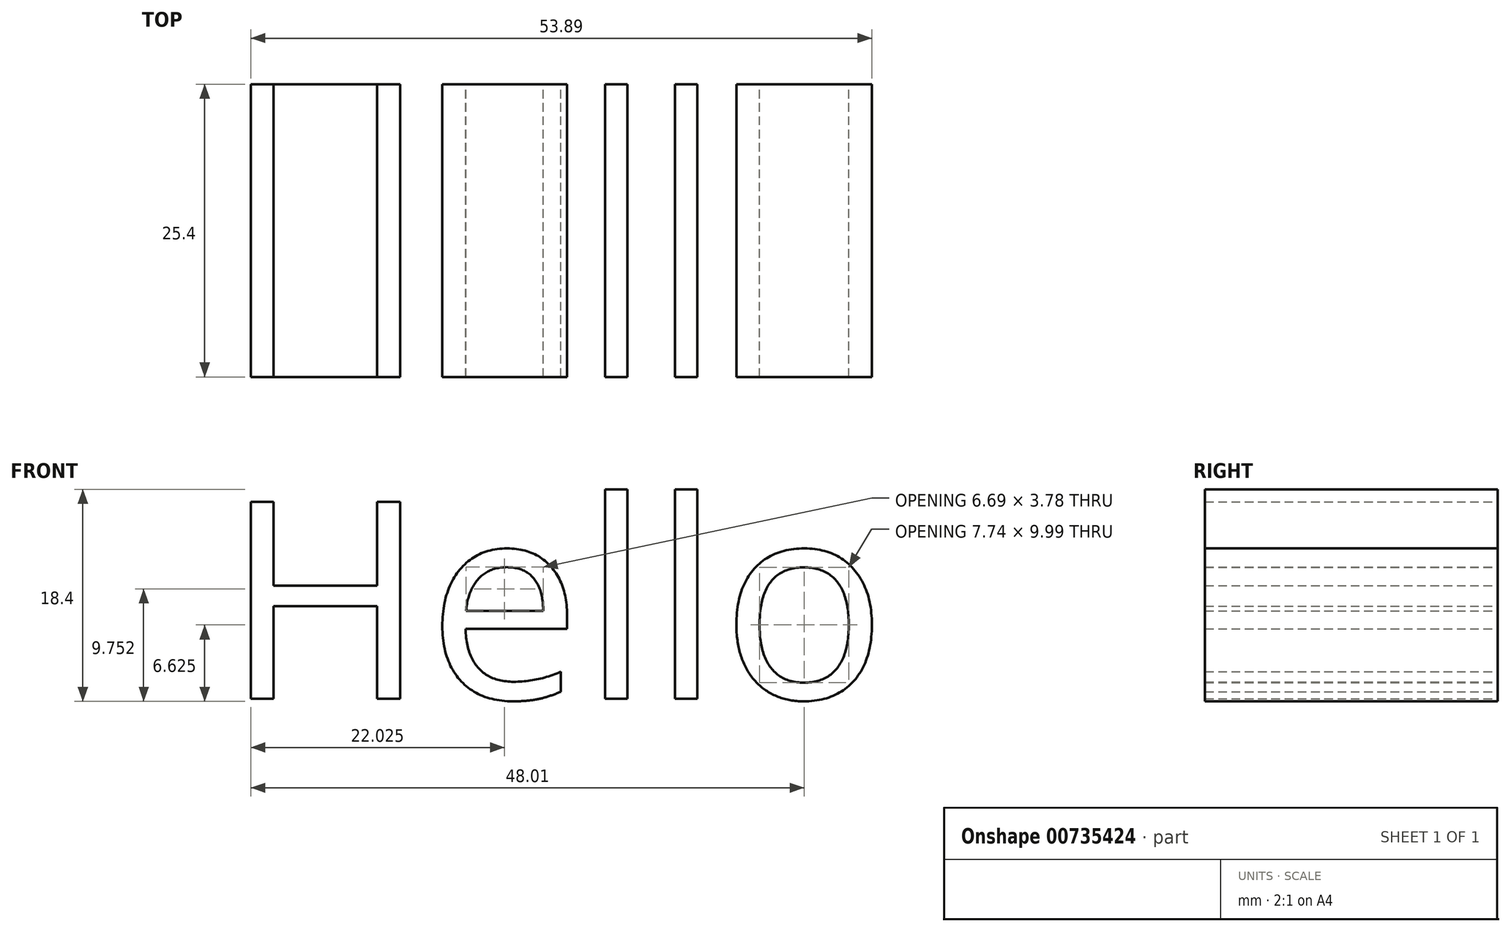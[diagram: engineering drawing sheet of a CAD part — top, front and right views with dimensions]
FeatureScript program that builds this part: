
annotation { "Feature Type Name" : "Feature", "Feature Type Description" : "" }
export const myFeature = defineFeature(function(context is Context, id is Id, definition is map)
    precondition{}
    {
        {
            var Q0;
            Q0=qCreatedBy(makeId("Front.planeOp"),FACE);
            var sketch = newSketch(context, id + "F0", { "sketchPlane" : qUnion([Q0])});
            skText(sketch, "E0", { "text": "Hello\n", "fontName": "OpenSans-Regular.ttf"});
            const initialGuessF0  = {"E0": [-0.0578, 0.00547, 1, 0, 0.01721]};
            skSetInitialGuess(sketch, initialGuessF0);
            skSolve(sketch);
        }
        {
            var Q0;
            Q0 = qSketchRegion(id + "F0", true);
            extrude(context, id + "F1", {"entities" : qUnion([Q0]), "depth" : 25.4 * mm, "offsetDistance" : 25.4 * mm});
        }
    });
